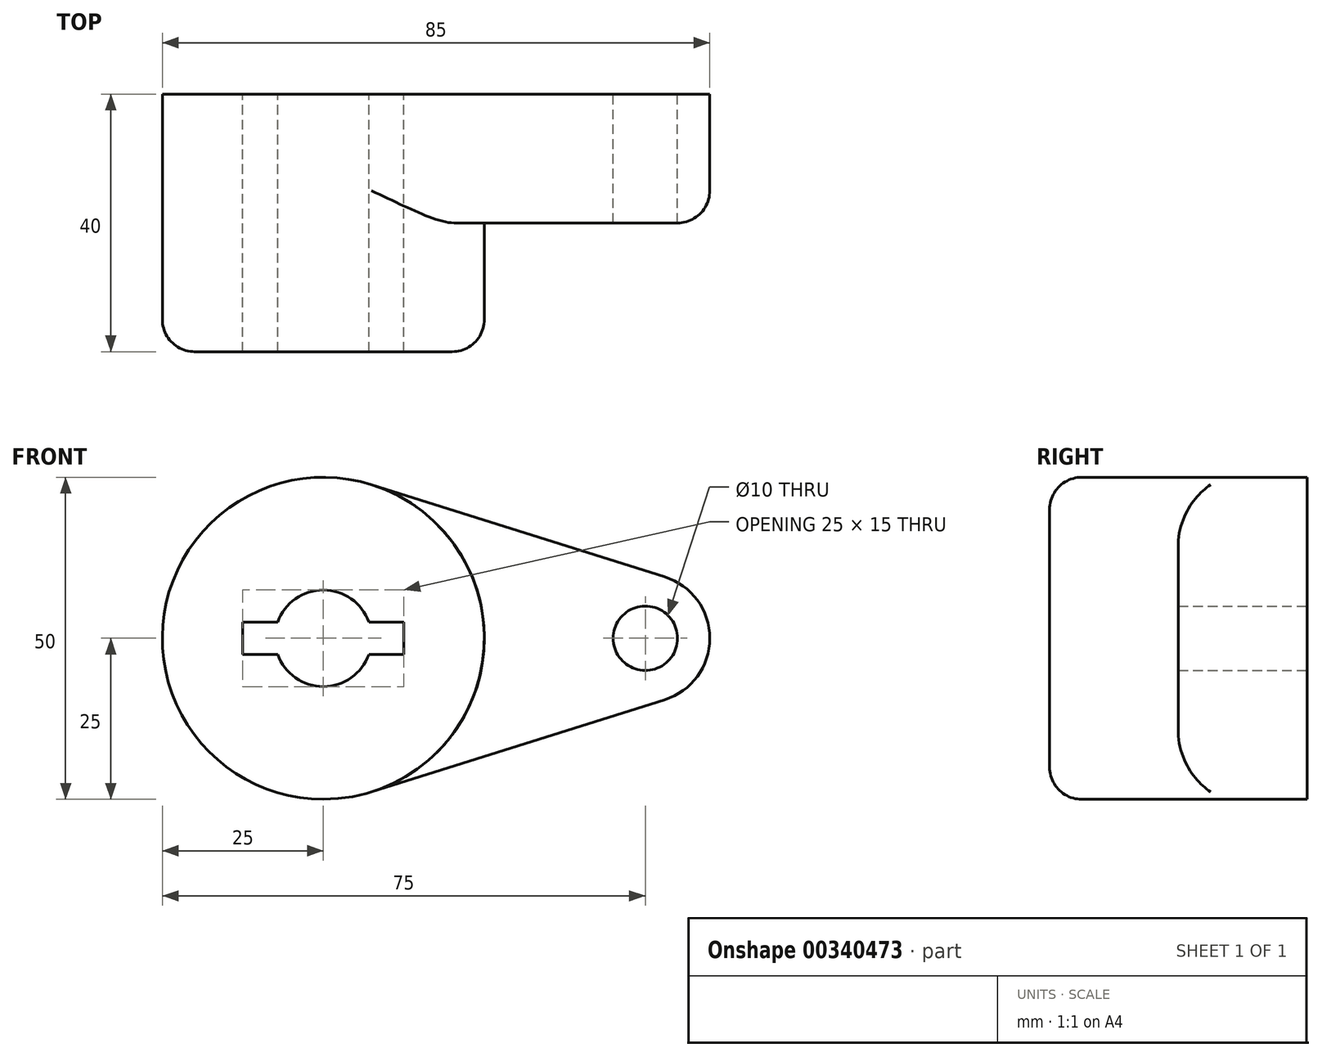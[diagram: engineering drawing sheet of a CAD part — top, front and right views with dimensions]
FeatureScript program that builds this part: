
annotation { "Feature Type Name" : "Feature", "Feature Type Description" : "" }
export const myFeature = defineFeature(function(context is Context, id is Id, definition is map)
    precondition{}
    {
        {
            var Q0;
            Q0=qCreatedBy(makeId("Front.planeOp"),FACE);
            var sketch = newSketch(context, id + "F0", { "sketchPlane" : qUnion([Q0])});
            skCircle(sketch, "E0", {"center": v(0, 0) * mm, "radius": 25 * mm});
            skCircle(sketch, "E1", {"center": v(50, 0) * mm, "radius": 10 * mm});
            skLineSegment(sketch, "E2", {"start": v(7.5, 23.85) * mm, "end": v(53, 9.54) * mm});
            skLineSegment(sketch, "E3", {"start": v(7.5, -23.85) * mm, "end": v(53, -9.54) * mm});
            skCircle(sketch, "E4", {"center": v(0, 0) * mm, "radius": 7.5 * mm});
            skCircle(sketch, "E5", {"center": v(50, 0) * mm, "radius": 5 * mm});
            skLineSegment(sketch, "E6.bottom", {"start": v(-12.5, -2.5) * mm, "end": v(12.5, -2.5) * mm});
            skLineSegment(sketch, "E6.top", {"start": v(-12.5, 2.5) * mm, "end": v(12.5, 2.5) * mm});
            skLineSegment(sketch, "E6.left", {"start": v(-12.5, -2.5) * mm, "end": v(-12.5, 2.5) * mm});
            skLineSegment(sketch, "E6.right", {"start": v(12.5, -2.5) * mm, "end": v(12.5, 2.5) * mm});
            skPoint(sketch, "E7", {"position": v(33, 9) * mm});
            skPoint(sketch, "E8", {"position": v(33, -9) * mm});
            skSolve(sketch);
        }
        {
            var Q0;
            {var subQ7=sQuery(id+"F0.wireOp",EDGE,"E6.left");Q0=makeQuery(id+"F0.imprint","IMPRINT",FACE,{"disambiguationData":[TD([[makeQuery(id+"F0.imprint","IMPRINT",EDGE,{"derivedFrom":subQ7}),1.0]])]});}
            extrude(context, id + "F1", {"entities" : qUnion([Q0]), "depth" : 40 * mm});
        }
        {
            var Q0;
            {var subQ0=sQuery(id+"F0.wireOp",EDGE,"E2");Q0=makeQuery(id+"F0.imprint","IMPRINT",FACE,{"disambiguationData":[TD([[makeQuery(id+"F0.imprint","IMPRINT",EDGE,{"derivedFrom":subQ0}),-1.0]])]});}
            var Q1;
            Q1=makeQuery(id+"F0.imprint","IMPRINT",FACE,{"disambiguationData":[TD([[makeQuery(id+"F0.imprint","IMPRINT",EDGE,{"derivedFrom":sQuery(id+"F0.wireOp",EDGE,"E5")}),-1.0]])]});
            extrude(context, id + "F2", {"entities" : qUnion([Q0, Q1]), "operationType" : NewBodyOperationType.ADD, "depth" : 20 * mm});
        }
        {
            var Q0;
            Q0=makeQuery(id+"F1.opExtrude","CAP_EDGE",EDGE,{"disambiguationData":[OSD([sQuery(id+"F0.wireOp",EDGE,"E0")])],"isStart":false});
            var Q1;
            Q1=makeQuery(id+"F2.opExtrude","CAP_EDGE",EDGE,{"disambiguationData":[OSD([sQuery(id+"F0.wireOp",EDGE,"E2")])],"isStart":false});
            fillet(context, id + "F3", {"entities" : qUnion([Q0, Q1]), "radius" : 5 * mm, "tangentPropagation" : true, "allowEdgeOverflow" : false});
        }
    });
